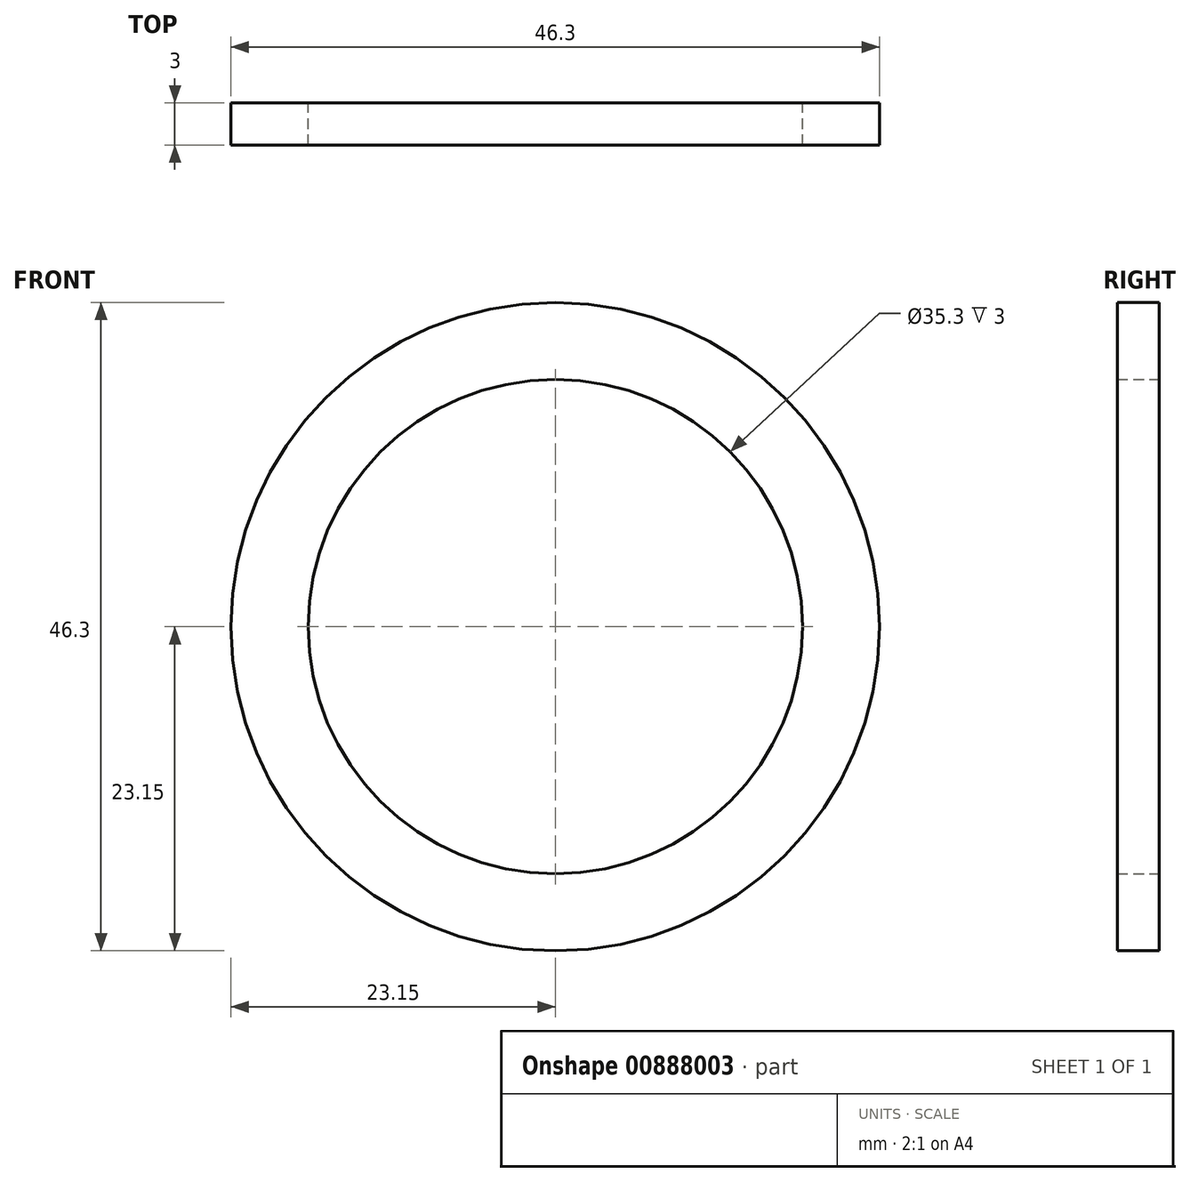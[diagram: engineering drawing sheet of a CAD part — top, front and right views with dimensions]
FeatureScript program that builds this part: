
annotation { "Feature Type Name" : "Feature", "Feature Type Description" : "" }
export const myFeature = defineFeature(function(context is Context, id is Id, definition is map)
    precondition{}
    {
        {
            var Q0;
            Q0=qCreatedBy(makeId("Front.planeOp"),FACE);
            var sketch = newSketch(context, id + "F0", { "sketchPlane" : qUnion([Q0])});
            skCircle(sketch, "E0", {"center": v(0, 0) * mm, "radius": 23.15 * mm});
            skCircle(sketch, "E1", {"center": v(0, 0) * mm, "radius": 17.65 * mm});
            skSolve(sketch);
        }
        {
            var Q0;
            Q0 = qSketchRegion(id + "F0", true);
            extrude(context, id + "F1", {"entities" : qUnion([Q0]), "depth" : 3 * mm, "offsetDistance" : 25 * mm});
        }
    });
